# Revit family: Pressure independent control valve 4006_M_SMART_LF_MF
name_source: partatom
category: Rohrzubehör
revit_build: Autodesk Revit 2018 (Build: 20190510_1515(x64)
units: mm (PartAtom-declared; Revit-internal decimal feet)

## family parameters
Arbeitsebenenbasiert = Nein
Beim Laden mit Abzugskörper schneiden = Nein
Bemaßung runder Anschluss = Durchmesser verwenden
Gemeinsam genutzt = Nein
Immer vertikal = Ja
OmniClass-Nummer = 23.65.55.14
OmniClass-Titel = Valves for Liquid Services
Teiletyp = Unterbricht

## types (2) — shared parameters
Application = the Pressure Independent Balancing Control Valve (PIBCV) is used in all heating and cooling systems with circulation pumps.
the valve automatically maintains flow to the required part of the system at the set rate by measuring and immediately adjusting to any variation in pressure.
no additional measurements are necessary and the correct flow rate is achieved at all operating conditions.
the diaphragm responds to the pressure upstream and downstream of the regulating valve (via an internal impulse line).
the valve settings directly affect the volumetric flow through the valve.
it is thus possible to set the maximum flow rate based on the flow chart when the valve is fitted.
this allows for the balancing of heating circuits, cooling water systems, ceiling cooling and heating panels, air heaters, etc. without any need to first assess the pressure variations in the system.
the valve‘s principal application is as a control valve for terminal units.
B01 = 50 mm
B02 = 45.4 mm
B03 = 44.372 mm
B04 = 41.901 mm
B05 = 40.933 mm
B06 = 39.471 mm
B07 = 30.908 mm
B08 = 23.556 mm  [stored 0.0772835 ft]
B09 = 7.998 mm  [stored 0.0262402 ft]
Capillary pipe = copper Cu-DHP (CW024A)
E01 = 23 mm  [stored 0.0754593 ft]
E02 = 20.014 mm  [stored 0.0656627 ft]
E03 = 18.385 mm  [stored 0.0603182 ft]
E04 = 19.704 mm  [stored 0.0646457 ft]
E05 = 20.519 mm  [stored 0.0673196 ft]
E06 = 17.921 mm  [stored 0.0587959 ft]
E07 = 5.15 mm
E08 = 20.825 mm  [stored 0.0683235 ft]
E09 = 20.075 mm  [stored 0.0658629 ft]
E10 = 20.427 mm  [stored 0.0670177 ft]
E11 = 10.7 mm  [stored 0.035105 ft]
E12 = 9.001 mm
E13 = 11.063 mm  [stored 0.0362959 ft]
E14 = 20.506 mm  [stored 0.0672769 ft]
E15 = 21.877 mm  [stored 0.0717749 ft]
E16 = 23.7 mm  [stored 0.0777559 ft]
E17 = 28.85 mm
E18 = 5.15 mm
E19 = 5 mm  [stored 0.0164042 ft]
E20 = 108.221 mm
H03 = 6.351 mm  [stored 0.0208366 ft]
H04 = 12 mm  [stored 0.0393701 ft]
Hersteller = Herz-Armaturen GmbH
Housing = DZR brass CC770S
L01 = 41 mm
L02 = 34 mm
L03 = 28 mm
L04 = 21 mm  [stored 0.0688976 ft]
L05 = 9 mm  [stored 0.0295276 ft]
L06 = 7 mm  [stored 0.0229659 ft]
Lift = 4 mm  [stored 0.0131234 ft]
Medium = water purity in accordance with the ÖNORM H5195 and VDI 2035 standards
the use of ethylene and propylene glycol in a mixture ratio of 25 - 50% by volume [%] is permitted.
Membrane = EPDM
Membrane housing = brass CW602N
O-Rings = EPDM
PN = 16
Pin = stainless steel 14301
Protective cap = plastic
R02 = 4.67 mm  [stored 0.0153215 ft]
R03 = 5.755 mm  [stored 0.0188812 ft]
R04 = 7.193 mm  [stored 0.0235991 ft]
R05 = 12.954 mm  [stored 0.0425 ft]
R06 = 22 mm  [stored 0.0721785 ft]
R07 = 18.816 mm  [stored 0.0617323 ft]
R08 = 13.212 mm  [stored 0.0433465 ft]
R09 = 16.292 mm  [stored 0.0534514 ft]
R10 = 6.8 mm  [stored 0.0223097 ft]
R11 = 9.62 mm  [stored 0.0315617 ft]
R12 = 6.8 mm  [stored 0.0223097 ft]
R13 = 3.496 mm
R14 = 8.07 mm
R15 = 7.225 mm  [stored 0.0237041 ft]
S08 = 30 mm
S09 = 10 mm  [stored 0.0328084 ft]
SCRNCODE = 05;04;02
SCRNSEQ = ARM;ARM_TYP="DURR";2
Spring = spring steel
URL = http://www.herzvalves.com
V10 = 7 mm  [stored 0.0229659 ft]
V12 = 17 mm
VRL01 = 30 mm
max. Operating pressure = 1600000.0 Pa
max. Operating temperature from DN40 = 110 °C
max. Operating temperature up to DN32 = 130 °C
min. Operating temperature (frost protection) = -20 °C
min. Operating temperature (pure water) = 2 °C

## type names (no varying parameters)
- LF
- MF

note: [stored X ft] marks values corroborated as IEEE doubles in the binary element streams (Revit-internal decimal feet)
